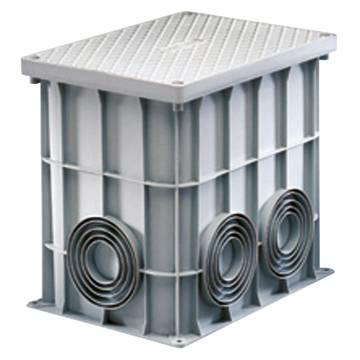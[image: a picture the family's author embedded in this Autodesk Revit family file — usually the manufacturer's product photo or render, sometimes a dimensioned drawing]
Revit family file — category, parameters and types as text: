
# Revit family: Building-Conduits-GEWISS-PU-ACCESS-CHAMBER-THERMOPLASTIC_RECTANGULAR
name_source: partatom
category: Attrezzatura elettrica
revit_build: Autodesk Revit 2016 (Build: 20161004_0715(x64)
units: mm (PartAtom-declared; Revit-internal decimal feet)

## family parameters
Condiviso = No
Configurazione quadro = Due colonne, circuiti in orizzontale
Host = Superficie
Numero OmniClass = 23.80.30.00
Punto di calcolo locali = Sì
Quota connettore circolare = Usa diametro
Taglio con vuoti quando caricato = No
Tipo di parte = Pannello comandi
Titolo OmniClass = Distribution Devices

## types (2) — shared parameters
Bordo acceso = Sì
Catalogue = BUILDING
Catalogue Range = PU
Colour = Grey
Dimension = 360x260x320 mm
Dimensions (mm) = 360x260x320 mm
Electrocod = 210
Finitura pozzetto = <Per categoria>
IDF = 5407318c-598f-4a9e-9dce-3dfd805534ef
IDT = 1b3f409b-8429-4d78-a2a3-a79cd94aa848
Immagine tipo = DX59502.jpg
Incasso pozzetto = 260 mm  [stored 0.853018 ft]
Larghezza_pozzetto = 360 mm  [stored 1.1811 ft]
Lunghezza pozzetto = 320 mm  [stored 1.04987 ft]
Produttore = GEWISS S.p.A.
Prospetto di default = 1219 mm
SEO = Well
Simbolo acceso = Sì
Technical sheet = https://www.gewiss.com
URL = https://www.gewiss.com
Version file RFA = 18.0

## per-type parameters (varying)
| type | Accessories supplied | Characteristics | Descrizione | EAN code | Modello |
| DX59502 - 360X260 PED. ACC. CHAMBER WITHOUT LID | 4 stainless steel screws | Flat semi-pierced base for boosting | 360X260 PED. ACC. CHAMBER WITHOUT LID | 8018678027948 | DX59502 |
| DX59501 - 360X260 H.R. ACC. CHAMBER - 360X260X320 | Cover high resistance and 4 S/Steel screws | Flat semi-pierced base | 360X260 H.R. ACC. CHAMBER - 360X260X320 | 8018678027924 | DX59501 |

note: [stored X ft] marks values corroborated as IEEE doubles in the binary element streams (Revit-internal decimal feet)

## geometry (parser evidence)
native form markers: Sweep x2
no freeform markers — native parametric forms only
